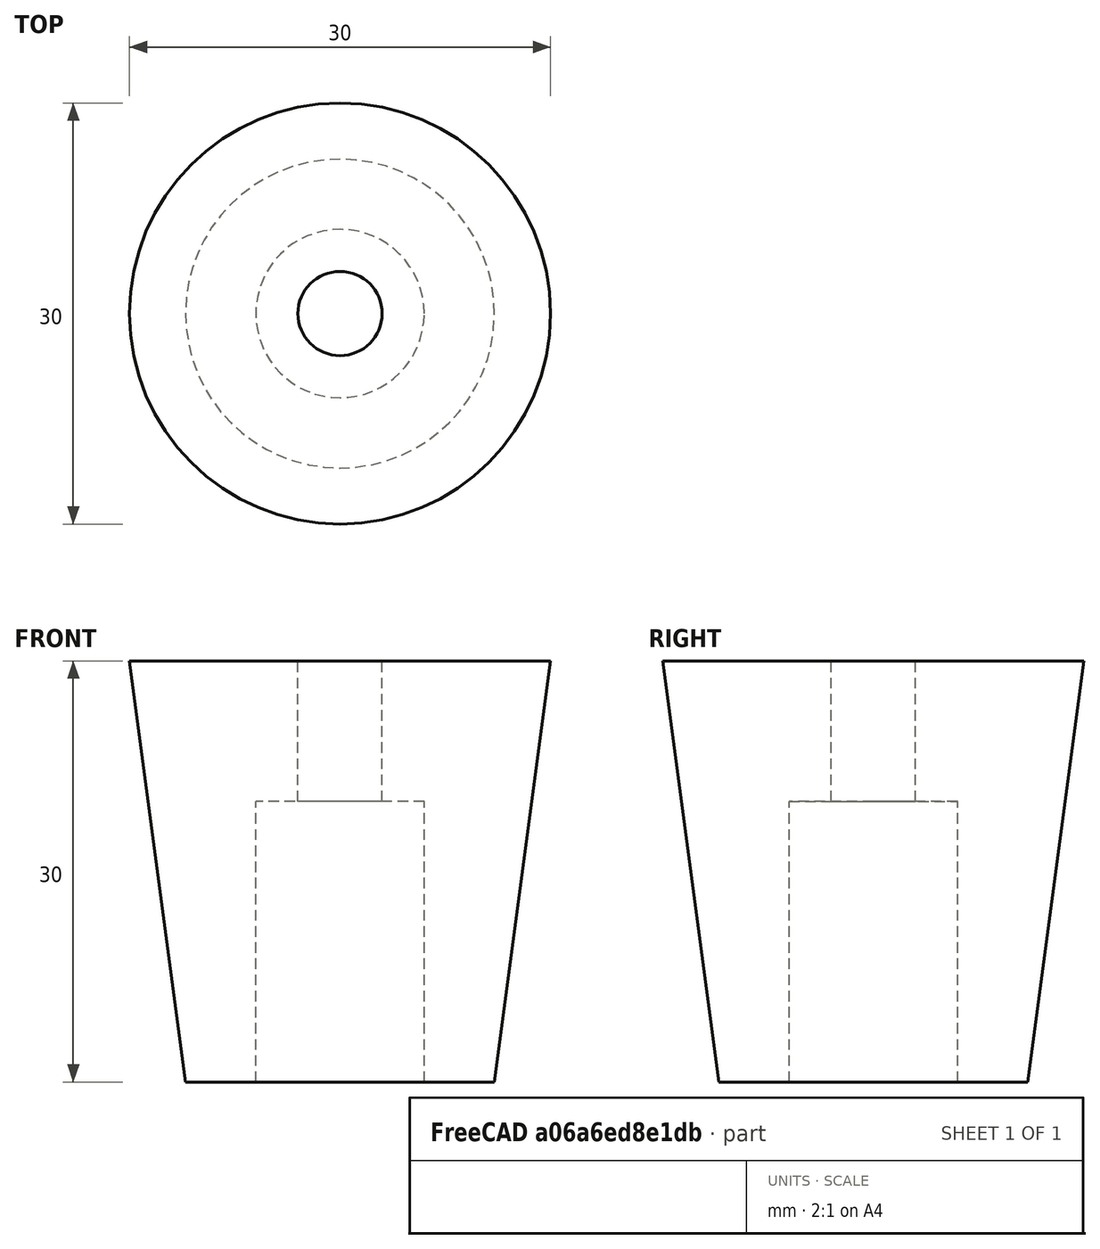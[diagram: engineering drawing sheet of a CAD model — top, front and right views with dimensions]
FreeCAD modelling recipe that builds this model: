
FCSTD DOCUMENT  (FreeCAD 0.19R21911 +2545 (Git))
Label: stopa
License: All rights reserved
LicenseURL: http://en.wikipedia.org/wiki/All_rights_reserved
objects: Sketcher::SketchObject×1, PartDesign::Revolution×1, PartDesign::Body×1
note: 5 computed .brp shape members not serialized (recipe doc carries the construction recipe); baked Part::Feature solids carry a one-line shape summary decoded from their .brp

FEATURE [Sketcher::SketchObject] Sketch
  MapMode = 5
  Placement = pos=(0,0,0) rot=(1,0,0;1.5708rad)
  Support = -> [XZ_Plane]
  sketch-geometry (6):
    g0: LineSegment StartX=3 StartY=0 StartZ=0 EndX=15 EndY=0 EndZ=0
    g1: LineSegment StartX=15 StartY=0 StartZ=0 EndX=11 EndY=-30 EndZ=0
    g2: LineSegment StartX=11 StartY=-30 StartZ=0 EndX=6 EndY=-30 EndZ=0
    g3: LineSegment StartX=6 StartY=-30 StartZ=0 EndX=6 EndY=-10 EndZ=0
    g4: LineSegment StartX=6 StartY=-10 StartZ=0 EndX=3 EndY=-10 EndZ=0
    g5: LineSegment StartX=3 StartY=-10 StartZ=0 EndX=3 EndY=0 EndZ=0
  constraints (18):
    c: Horizontal(g0)
    c: Coincident(g0,g1)
    c: Coincident(g1,g2)
    c: Horizontal(g2)
    c: Coincident(g2,g3)
    c: Vertical(g3)
    c: Coincident(g3,g4)
    c: Horizontal(g4)
    c: Coincident(g4,g5)
    c: Coincident(g0,g5)
    c: Vertical(g5)
    c: DistanceX(g-1,g0) = 15
    c: DistanceX(g-1,g1) = 11
    c: DistanceY(g1,g0) = 30
    c: PointOnObject(g0,g-1)
    c: DistanceX(g2) = 6
    c: DistanceX(g4) = 3
    c: DistanceY(g3,g3) = 20
FEATURE [PartDesign::Revolution] Revolution
  AllowMultiFace = false
  Angle = 360
  Axis = (0,-1.035e-13,1)
  Base = (0,0,0)
  ClaimChildren = false
  Placement = pos=(0,0,0) rot=(1,0,0;1.5708rad)
  Profile = -> Sketch
  ReferenceAxis = -> Sketch [V_Axis]
  Reversed = true
  Suppress = false
FEATURE [PartDesign::Body] Body  label="stopa"
  ExportMode = 0
  Group = -> [Sketch,Revolution]
  Origin = -> Origin
  SingleSolid = true
  Tip = -> Revolution
  _ExportChildren = -> [Revolution]
  _GroupVersion = 1
